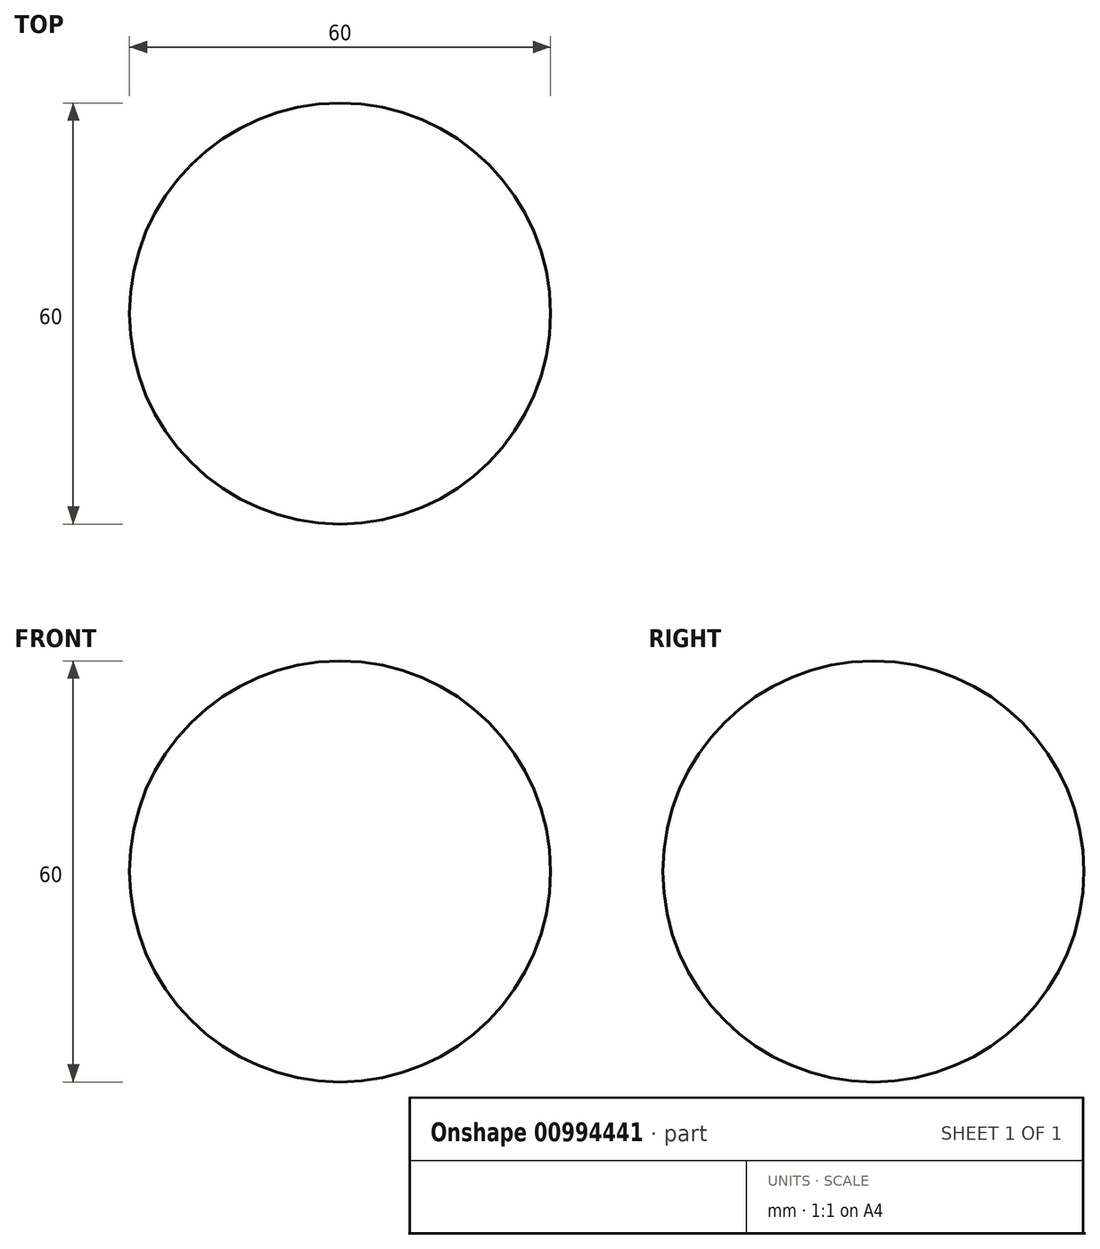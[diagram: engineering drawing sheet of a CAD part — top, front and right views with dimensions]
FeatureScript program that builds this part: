
annotation { "Feature Type Name" : "Feature", "Feature Type Description" : "" }
export const myFeature = defineFeature(function(context is Context, id is Id, definition is map)
    precondition{}
    {
        {
            var Q0;
            Q0=qCreatedBy(makeId("Top.planeOp"),FACE);
            var sketch = newSketch(context, id + "F0", { "sketchPlane" : qUnion([Q0])});
            skLineSegment(sketch, "E0", {"start": v(0, 52.48) * mm, "end": v(0, -51.5) * mm});
            skArc(sketch, "E1", {"start": v(0, 30) * mm, "mid": v(-30, 0) * mm, "end": v(0, -30) * mm});
            skSolve(sketch);
        }
        {
            var Q0;
            {var subQ0=sQuery(id+"F0.wireOp",EDGE,"E1");Q0=makeQuery(id+"F0.imprint","IMPRINT",FACE,{"disambiguationData":[TD([[makeQuery(id+"F0.imprint","IMPRINT",EDGE,{"derivedFrom":subQ0}),1.0]])]});}
            var Q1;
            Q1=sQuery(id+"F0.wireOp",EDGE,"E0");
            revolve(context, id + "F1", {"surfaceOperationType" : NewSurfaceOperationType.NEW, "entities" : qUnion([Q0]), "axis" : qUnion([Q1]), "revolveType" : RevolveType.FULL});
        }
    });
